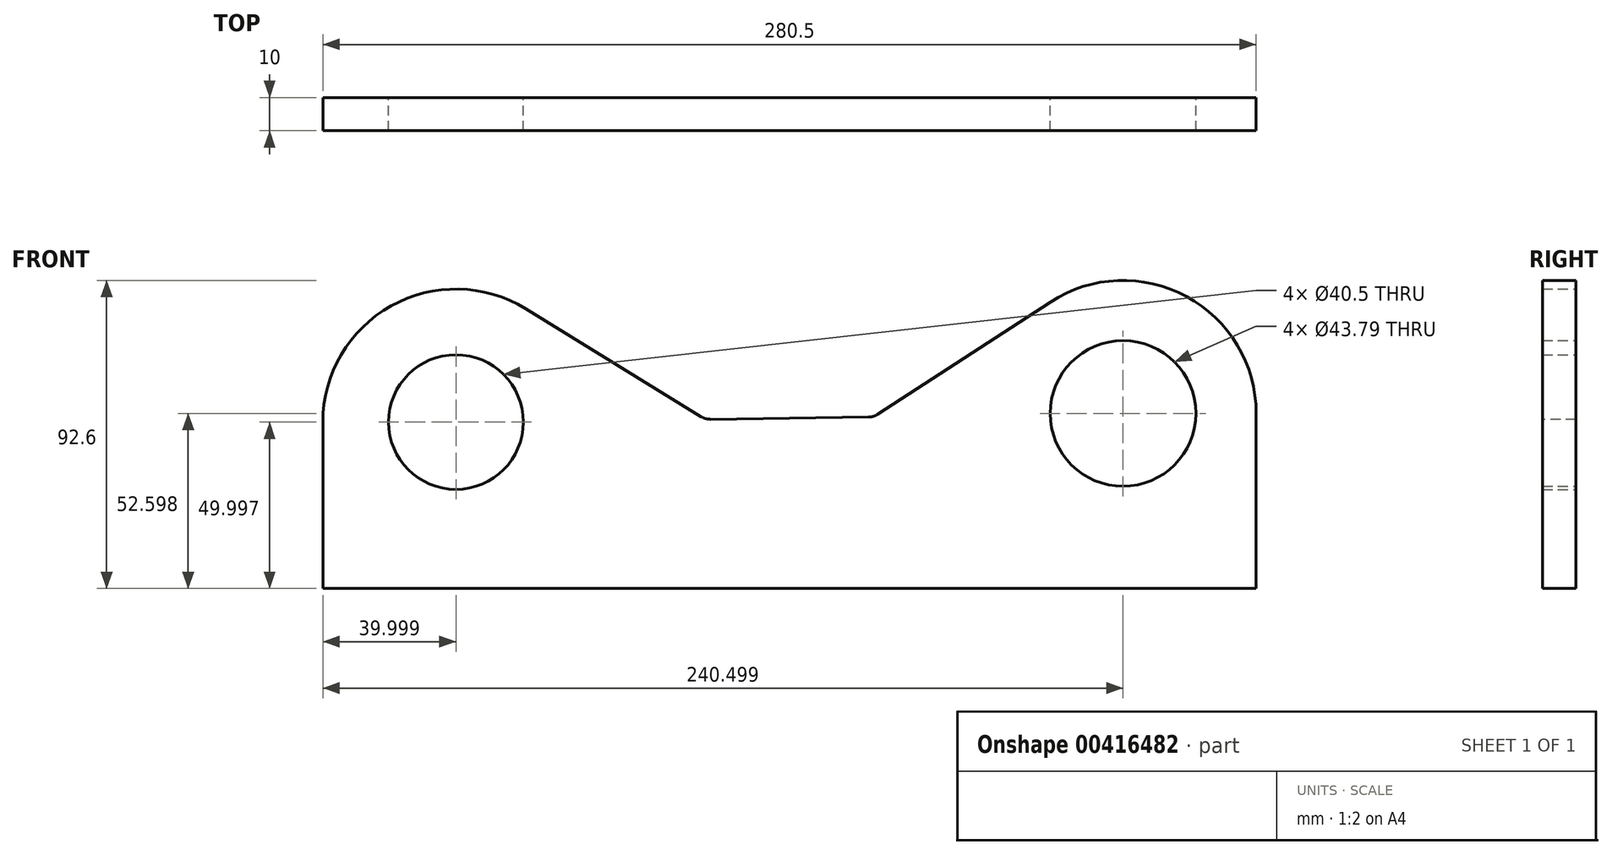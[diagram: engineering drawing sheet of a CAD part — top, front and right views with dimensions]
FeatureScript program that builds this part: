
annotation { "Feature Type Name" : "Feature", "Feature Type Description" : "" }
export const myFeature = defineFeature(function(context is Context, id is Id, definition is map)
    precondition{}
    {
        {
            var Q0;
            Q0=qCreatedBy(makeId("Front.planeOp"),FACE);
            var sketch = newSketch(context, id + "F0", { "sketchPlane" : qUnion([Q0])});
            skCircle(sketch, "E0", {"center": v(-62.07, 19.7) * mm, "radius": 20.25 * mm});
            skCircle(sketch, "E1", {"center": v(138.43, 22.3) * mm, "radius": 21.9 * mm});
            skArc(sketch, "E2", {"start": v(-41.11, 53.78) * mm, "mid": v(-81.59, 54.62) * mm, "end": v(-102.07, 19.7) * mm});
            skArc(sketch, "E3", {"start": v(178.43, 22.3) * mm, "mid": v(157.5, 57.47) * mm, "end": v(116.62, 55.84) * mm});
            skLineSegment(sketch, "E4.trimOffspring", {"start": v(12.93, 20.53) * mm, "end": v(63.43, 21.25) * mm});
            skLineSegment(sketch, "E5", {"start": v(116.62, 55.84) * mm, "end": v(63.43, 21.25) * mm});
            skLineSegment(sketch, "E6", {"start": v(-41.11, 53.78) * mm, "end": v(12.93, 20.53) * mm});
            skLineSegment(sketch, "E7", {"start": v(-102.07, -30.3) * mm, "end": v(178.43, -30.3) * mm});
            skLineSegment(sketch, "E8", {"start": v(-102.07, -30.3) * mm, "end": v(-102.07, 19.7) * mm});
            skLineSegment(sketch, "E9", {"start": v(178.43, -30.3) * mm, "end": v(178.43, 22.3) * mm});
            skPoint(sketch, "E10.orphan", {"position": v(98.43, 21.74) * mm});
            skPoint(sketch, "E11.orphan", {"position": v(-22.07, 20.04) * mm});
            skSolve(sketch);
        }
        {
            var Q0;
            Q0=makeQuery(id+"F0.imprint","IMPRINT",FACE,{"disambiguationData":[TD([[makeQuery(id+"F0.imprint","IMPRINT",EDGE,{"derivedFrom":sQuery(id+"F0.wireOp",EDGE,"E0")}),-1.0]])]});
            extrude(context, id + "F1", {"entities" : qUnion([Q0]), "depth" : 10 * mm});
        }
        {
            var Q0;
            Q0=makeQuery(id+"F1.opExtrude","SWEPT_EDGE",EDGE,{"disambiguationData":[OSD([sQuery(id+"F0.wireOp",EDGE,"E4.trimOffspring"),sQuery(id+"F0.wireOp",EDGE,"E6")])]});
            var Q1;
            Q1=makeQuery(id+"F1.opExtrude","SWEPT_EDGE",EDGE,{"disambiguationData":[OSD([sQuery(id+"F0.wireOp",EDGE,"E4.trimOffspring"),sQuery(id+"F0.wireOp",EDGE,"E5")])]});
            fillet(context, id + "F2", {"entities" : qUnion([Q0, Q1]), "radius" : 5 * mm, "tangentPropagation" : true, "allowEdgeOverflow" : false});
        }
    });
